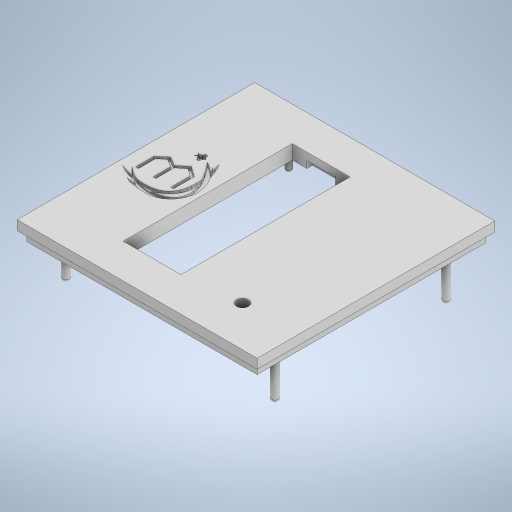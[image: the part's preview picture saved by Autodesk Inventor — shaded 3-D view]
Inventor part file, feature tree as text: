
AUTODESK INVENTOR PART (.ipt)
format: ipt  version: 2023 (Build 270158000, 158)  size: 964,096 bytes
history: native  units: mm
features: extrude x13, sketch x8, fillet x2, other x1
ambient origin geometry x8: Origin, YZ Plane, XZ Plane, XY Plane, X Axis, Y Axis, Z Axis, Center Point
bodies: Body1 (feature_tree)
feature tree (24):
  other  "Sólido1"
  extrude  "Base"  Depth=100.0mm
  extrude  "Pinos_encaixe"  Depth=71.15mm
  fillet  "Arredondamento_pino"  Radius=8.0mm
  extrude  "Logo Iobee C.1"  Depth=3.0mm
  extrude  "Logo Iobee C.2"  Depth=3.0mm TaperAngle=0.0deg
  extrude  "Logo Iobee C.3"  Depth=1.5mm TaperAngle=0.0deg
  sketch  "Esboço_ESP32"  dims[d34=28.0mm d35=60.0mm]
  extrude  "ESP32_alocar"  Depth=0.5mm TaperAngle=0.0deg
  extrude  "ESP32_Wi-Fi"  Depth=60.0mm
  extrude  "LCD_Dentro"  Depth=8.0mm
  sketch  "Esboço7"  dims[d2=24.3mm d3=71.15mm d4=8.0mm d5=0.0mm]
  extrude  "Chaveta_LCD"  Depth=4.5mm
  extrude  "LCD Pinos"  Depth=5.0mm TaperAngle=0.0deg
  extrude  "Rasgo de Encaixe"  Depth=3.0mm TaperAngle=0.0deg
  sketch  "Esboço9"  dims[d23=3.0mm d24=3.0mm d25=18.0mm d26=0.0mm]
  extrude  "Pinos Guia LCD"  Depth=36.05mm
  fillet  "Arredondamento2"  Radius=79.9mm
  extrude  "Furo Led"  Depth=2.0mm TaperAngle=0.0deg
  sketch  "Esboço4"  dims[d0=101.0mm d1=100.0mm]
  sketch  "Esboço_LCD_dentro"  dims[d36=19.0mm d37=8.0mm d38=4.5mm d39=5.0mm d40=0.0mm d42=3.0mm d43=0.0mm d44=36.05mm d45=79.9mm d46=2.0mm d47=0.0mm d52=3.0mm d53=0.0mm d54=4.0mm d55=40.0mm d56=6.2mm d57=4.0mm d58=0.0mm d60=4.0mm d61=0.0mm d68=2.5mm d69=2.5mm d70=2.5mm d71=2.5mm d73=75.9mm d74=7.0mm d75=0.0mm d76=1.0mm d77=5.0mm d78=0.0mm d79=0.0mm d80=96.0mm d81=97.0mm d82=6.5mm d83=14.0mm d84=9.2mm d86=32.05mm d88=2.0mm d50=0.5mm d51=0.872665mm]
  sketch  "Esboço8"  dims[d21=3.0mm d22=3.0mm]
  sketch  "Esboço10"  dims[d27=1.5mm d28=1.5mm d29=0.0mm]
  sketch  "Esboço11"  dims[d30=1.0mm d31=0.0mm d32=0.5mm d33=0.0mm]
